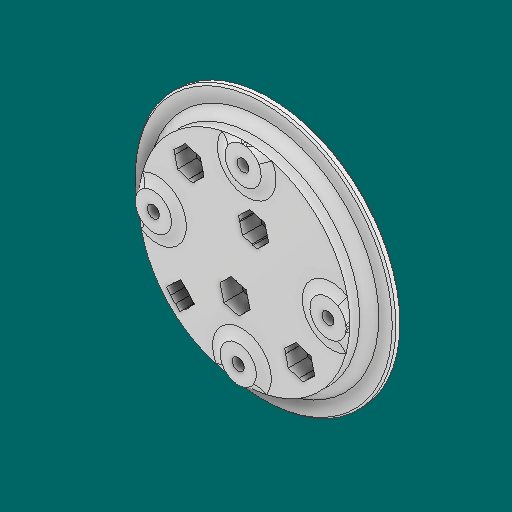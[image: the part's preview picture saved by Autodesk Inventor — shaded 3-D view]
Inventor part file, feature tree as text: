
AUTODESK INVENTOR PART (.ipt)
format: ipt  version: 2023.1 (Build 271208000, 208)  size: 650,240 bytes
history: native  units: in
note: dims shown in document units (in); Inventor stores cm internally (conversion verified against a paired STEP export)
features: sketch x6, other x3
ambient origin geometry x8: Origin, YZ Plane, XZ Plane, XY Plane, X Axis, Y Axis, Z Axis, Center Point
bodies: Solid1 (feature_tree)
feature tree (9):
  other  "SteeringCoupler.ipt"
  other  "Solid1::SteeringCoupler.ipt"
  other  "TaggingFeature1"
  sketch  "Sketch1"  dims[d0=0.3937in]
  sketch  "Sketch2"
  sketch  "Sketch4"
  sketch  "Sketch5"
  sketch  "Sketch6"
  sketch  "Sketch8"
